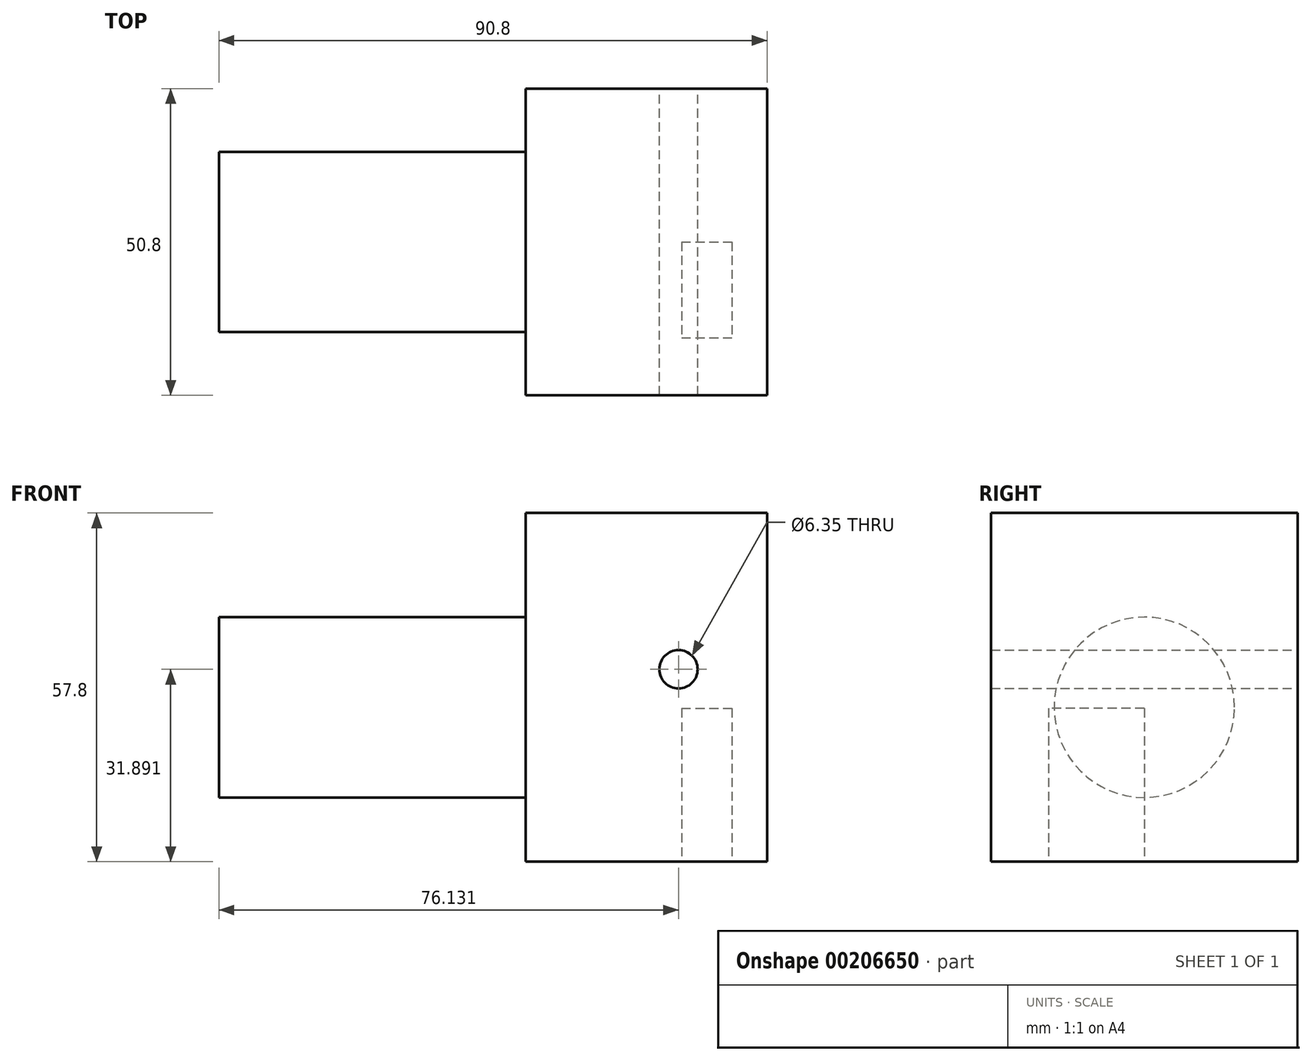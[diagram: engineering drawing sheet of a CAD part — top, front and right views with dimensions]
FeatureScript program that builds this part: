
annotation { "Feature Type Name" : "Feature", "Feature Type Description" : "" }
export const myFeature = defineFeature(function(context is Context, id is Id, definition is map)
    precondition{}
    {
        {
            var Q0;
            Q0=qCreatedBy(makeId("Front.planeOp"),FACE);
            var sketch = newSketch(context, id + "F0", { "sketchPlane" : qUnion([Q0])});
            skLineSegment(sketch, "E0.bottom", {"start": v(-45.4, 28.9) * mm, "end": v(45.4, 28.9) * mm});
            skLineSegment(sketch, "E0.top", {"start": v(-45.4, -28.9) * mm, "end": v(45.4, -28.9) * mm});
            skLineSegment(sketch, "E0.left", {"start": v(-45.4, 28.9) * mm, "end": v(-45.4, -28.9) * mm});
            skLineSegment(sketch, "E0.right", {"start": v(45.4, 28.9) * mm, "end": v(45.4, -28.9) * mm});
            skPoint(sketch, "E0.middle", {"position": v(0, 0) * mm});
            skSolve(sketch);
        }
        {
            var Q0;
            Q0 = qSketchRegion(id + "F0", true);
            extrude(context, id + "F1", {"entities" : qUnion([Q0]), "endBound" : BoundingType.SYMMETRIC, "depth" : 50.8 * mm});
        }
        {
            var Q0;
            Q0=makeQuery(id+"F1.opExtrude","SWEPT_FACE",FACE,{"disambiguationData":[OSD([sQuery(id+"F0.wireOp",EDGE,"E0.left")])]});
            var sketch = newSketch(context, id + "F2", { "sketchPlane" : qUnion([Q0])});
            skCircle(sketch, "E1", {"center": v(0, -3.3) * mm, "radius": 14.94 * mm});
            skSolve(sketch);
        }
        {
            var Q0;
            Q0=makeQuery(id+"F2.imprint","IMPRINT",FACE,{"disambiguationData":[TD([[makeQuery(id+"F2.imprint","IMPRINT",EDGE,{"derivedFrom":sQuery(id+"F2.wireOp",EDGE,"E1")}),-1.0]])]});
            extrude(context, id + "F3", {"entities" : qUnion([Q0]), "operationType" : NewBodyOperationType.REMOVE, "oppositeDirection" : true, "depth" : 50.8 * mm});
        }
        {
            var Q0;
            Q0=makeQuery(id+"F1.opExtrude","CAP_FACE",FACE,{"disambiguationData":[OSD([sQuery(id+"F0.wireOp",EDGE,"E0.bottom"),sQuery(id+"F0.wireOp",EDGE,"E0.top"),sQuery(id+"F0.wireOp",EDGE,"E0.left"),sQuery(id+"F0.wireOp",EDGE,"E0.right")])],"isStart":true});
            var sketch = newSketch(context, id + "F4", { "sketchPlane" : qUnion([Q0])});
            skCircle(sketch, "E2", {"center": v(-30.73, 3) * mm, "radius": 6.88 * mm});
            skSolve(sketch);
        }
        {
            var Q0;
            Q0=sQuery(id+"F4.wireOp",VERTEX,"E2.center");
            var Q1;
            Q1=makeQuery(id+"F1.opExtrude","SWEPT_BODY",BODY,{"disambiguationData":[OSD([sQuery(id+"F0.wireOp",EDGE,"E0.bottom"),sQuery(id+"F0.wireOp",EDGE,"E0.top"),sQuery(id+"F0.wireOp",EDGE,"E0.left"),sQuery(id+"F0.wireOp",EDGE,"E0.right")])]});
            hole(context, id + "F5", {"style" : HoleStyle.SIMPLE, "endStyle" : HoleEndStyle.THROUGH, "holeDiameter" : 6.35 * mm, "locations" : qUnion([Q0]), "scope" : qUnion([Q1]), "isTappedThrough" : true});
        }
        {
            var Q0;
            Q0=makeQuery(id+"F1.opExtrude","SWEPT_FACE",FACE,{"disambiguationData":[OSD([sQuery(id+"F0.wireOp",EDGE,"E0.top")])]});
            var sketch = newSketch(context, id + "F6", { "sketchPlane" : qUnion([Q0])});
            skLineSegment(sketch, "E3.bottom", {"start": v(31.24, 0) * mm, "end": v(39.59, 0) * mm});
            skLineSegment(sketch, "E3.top", {"start": v(31.24, 15.88) * mm, "end": v(39.59, 15.88) * mm});
            skLineSegment(sketch, "E3.left", {"start": v(31.24, 0) * mm, "end": v(31.24, 15.88) * mm});
            skLineSegment(sketch, "E3.right", {"start": v(39.59, 0) * mm, "end": v(39.59, 15.88) * mm});
            skPoint(sketch, "E3.middle", {"position": v(35.41, 7.94) * mm});
            skSolve(sketch);
        }
        {
            var Q0;
            Q0 = qSketchRegion(id + "F6", true);
            extrude(context, id + "F7", {"entities" : qUnion([Q0]), "operationType" : NewBodyOperationType.REMOVE, "oppositeDirection" : true, "depth" : 25.4 * mm});
        }
    });
